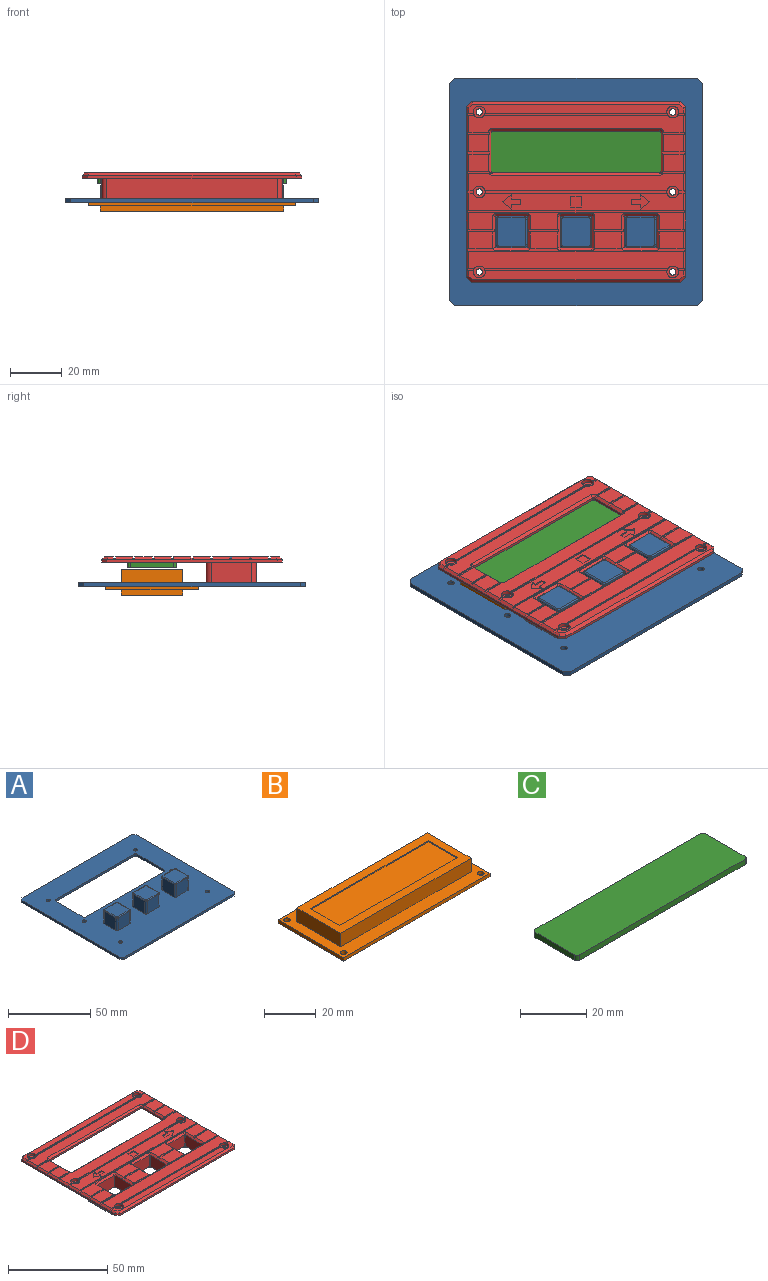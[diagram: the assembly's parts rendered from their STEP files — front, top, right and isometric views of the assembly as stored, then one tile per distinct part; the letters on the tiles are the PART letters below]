
ASSEMBLY  parts=4 mates=3
PART A: 75 faces, bbox 98x88x11.6 mm
  f0: plane 98x88mm, normal (0,0,1), area 6339.1mm2, adj f2,f3,f4,f5,f6,f7,f8,f9
  f1: plane 98x88mm, normal (0,0,-1), area 6768.5mm2, adj f2,f3,f4,f5,f6,f7,f8,f9
  f2: plane 94x1.6mm, normal (0,-1,0), area 150.4mm2, adj f0,f1,f64,f65
  f3: plane 84x1.6mm, normal (1,0,0), area 134.4mm2, adj f0,f1,f65,f66
  f4: plane 94x1.6mm, normal (0,1,0), area 150.4mm2, adj f0,f1,f63,f66
  f5: plane 84x1.6mm, normal (-1,0,0), area 134.4mm2, adj f0,f1,f63,f64
  f6: cylinder r=1.25mm len=2.5mm, axis (0,0,1), area 12.6mm2, adj f0,f1
  f7: cylinder r=1.25mm len=2.5mm, axis (0,0,1), area 12.6mm2, adj f0,f1
  f8: cylinder r=1.25mm len=2.5mm, axis (0,0,1), area 12.6mm2, adj f0,f1
  f9: cylinder r=1.25mm len=2.5mm, axis (0,0,1), area 12.6mm2, adj f0,f1
  f10: cylinder r=1.25mm len=2.5mm, axis (0,0,1), area 12.6mm2, adj f0,f1
  f11: cylinder r=1.25mm len=2.5mm, axis (0,0,1), area 12.6mm2, adj f0,f1
  f12: plane 10x9.5mm, normal (0,-1,0), area 95mm2, adj f0,f35,f38,f45
  f13: plane 10x9.5mm, normal (1,0,0), area 95mm2, adj f0,f37,f38,f41
  f14: plane 10x9.5mm, normal (0,1,0), area 95mm2, adj f0,f36,f37,f40
  f15: plane 10x9.5mm, normal (-1,0,0), area 95mm2, adj f0,f35,f36,f44
  f16: plane 11x11mm, normal (0,0,1), area 120.8mm2, adj f39,f40,f41,f42,f43,f44,f45,f46
  f17: plane 10x9.5mm, normal (-1,0,0), area 95mm2, adj f0,f31,f34,f52
  f18: plane 10x9.5mm, normal (0,-1,0), area 95mm2, adj f0,f31,f32,f53
  f19: plane 10x9.5mm, normal (1,0,0), area 95mm2, adj f0,f32,f33,f49
  f20: plane 10x9.5mm, normal (0,1,0), area 95mm2, adj f0,f33,f34,f48
  f21: plane 11x11mm, normal (0,0,1), area 120.8mm2, adj f47,f48,f49,f50,f51,f52,f53,f54
  f22: plane 10x9.5mm, normal (0,1,0), area 95mm2, adj f0,f27,f30,f61
  f23: plane 10x9.5mm, normal (-1,0,0), area 95mm2, adj f0,f29,f30,f57
  f24: plane 10x9.5mm, normal (0,-1,0), area 95mm2, adj f0,f28,f29,f56
  f25: plane 10x9.5mm, normal (1,0,0), area 95mm2, adj f0,f27,f28,f60
  f26: plane 11x11mm, normal (0,0,1), area 120.8mm2, adj f55,f56,f57,f58,f59,f60,f61,f62
  f27: cylinder r=1mm len=9.5mm, axis (0,0,-1), area 14.9mm2, adj f0,f22,f25,f62
  f28: cylinder r=1mm len=9.5mm, axis (0,0,1), area 14.9mm2, adj f0,f24,f25,f58
  f29: cylinder r=1mm len=9.5mm, axis (0,0,-1), area 14.9mm2, adj f0,f23,f24,f55
  f30: cylinder r=1mm len=9.5mm, axis (0,0,1), area 14.9mm2, adj f0,f22,f23,f59
  f31: cylinder r=1mm len=9.5mm, axis (0,0,1), area 14.9mm2, adj f0,f17,f18,f54
  f32: cylinder r=1mm len=9.5mm, axis (0,0,-1), area 14.9mm2, adj f0,f18,f19,f51
  f33: cylinder r=1mm len=9.5mm, axis (0,0,1), area 14.9mm2, adj f0,f19,f20,f47
  f34: cylinder r=1mm len=9.5mm, axis (0,0,-1), area 14.9mm2, adj f0,f17,f20,f50
  f35: cylinder r=1mm len=9.5mm, axis (0,0,-1), area 14.9mm2, adj f0,f12,f15,f46
  f36: cylinder r=1mm len=9.5mm, axis (0,0,1), area 14.9mm2, adj f0,f14,f15,f42
  f37: cylinder r=1mm len=9.5mm, axis (0,0,-1), area 14.9mm2, adj f0,f13,f14,f39
  f38: cylinder r=1mm len=9.5mm, axis (0,0,1), area 14.9mm2, adj f0,f12,f13,f43
  f39: torus R=0.5mm, axis (0,0,1), area 1mm2, adj f16,f37,f40,f41
  f40: cylinder r=0.5mm len=10mm, axis (1,0,0), area 7.9mm2, adj f14,f16,f39,f42
  f41: cylinder r=0.5mm len=10mm, axis (0,-1,0), area 7.9mm2, adj f13,f16,f39,f43
  f42: torus R=0.5mm, axis (0,0,1), area 1mm2, adj f16,f36,f40,f44
  f43: torus R=0.5mm, axis (0,0,1), area 1mm2, adj f16,f38,f41,f45
  f44: cylinder r=0.5mm len=10mm, axis (0,1,0), area 7.9mm2, adj f15,f16,f42,f46
  f45: cylinder r=0.5mm len=10mm, axis (-1,0,0), area 7.9mm2, adj f12,f16,f43,f46
  f46: torus R=0.5mm, axis (0,0,1), area 1mm2, adj f16,f35,f44,f45
  f47: torus R=0.5mm, axis (0,0,1), area 1mm2, adj f21,f33,f48,f49
  f48: cylinder r=0.5mm len=10mm, axis (1,0,0), area 7.9mm2, adj f20,f21,f47,f50
  f49: cylinder r=0.5mm len=10mm, axis (0,-1,0), area 7.9mm2, adj f19,f21,f47,f51
  f50: torus R=0.5mm, axis (0,0,1), area 1mm2, adj f21,f34,f48,f52
  f51: torus R=0.5mm, axis (0,0,1), area 1mm2, adj f21,f32,f49,f53
  f52: cylinder r=0.5mm len=10mm, axis (0,1,0), area 7.9mm2, adj f17,f21,f50,f54
  f53: cylinder r=0.5mm len=10mm, axis (-1,0,0), area 7.9mm2, adj f18,f21,f51,f54
  f54: torus R=0.5mm, axis (0,0,1), area 1mm2, adj f21,f31,f52,f53
  f55: torus R=0.5mm, axis (0,0,1), area 1mm2, adj f26,f29,f56,f57
  f56: cylinder r=0.5mm len=10mm, axis (-1,0,0), area 7.9mm2, adj f24,f26,f55,f58
  f57: cylinder r=0.5mm len=10mm, axis (0,1,0), area 7.9mm2, adj f23,f26,f55,f59
  f58: torus R=0.5mm, axis (0,0,1), area 1mm2, adj f26,f28,f56,f60
  f59: torus R=0.5mm, axis (0,0,1), area 1mm2, adj f26,f30,f57,f61
  f60: cylinder r=0.5mm len=10mm, axis (0,-1,0), area 7.9mm2, adj f25,f26,f58,f62
  f61: cylinder r=0.5mm len=10mm, axis (1,0,0), area 7.9mm2, adj f22,f26,f59,f62
  f62: torus R=0.5mm, axis (0,0,1), area 1mm2, adj f26,f27,f60,f61
  f63: plane 2x2mm, normal (-0.71,0.71,0), area 4.5mm2, adj f0,f1,f4,f5
  f64: plane 2x2mm, normal (-0.71,-0.71,0), area 4.5mm2, adj f0,f1,f2,f5
  f65: plane 2x2mm, normal (0.71,-0.71,0), area 4.5mm2, adj f0,f1,f2,f3
  f66: plane 2x2mm, normal (0.71,0.71,0), area 4.5mm2, adj f0,f1,f3,f4
  f67: plane 68x1.6mm, normal (0,1,0), area 108.8mm2, adj f0,f1,f71,f72
  f68: plane 24x1.6mm, normal (-1,0,0), area 38.4mm2, adj f0,f1,f72,f73
  f69: plane 68x1.6mm, normal (0,-1,0), area 108.8mm2, adj f0,f1,f73,f74
  f70: plane 24x1.6mm, normal (1,0,0), area 38.4mm2, adj f0,f1,f71,f74
  f71: plane 1.6x1mm, normal (0.71,0.71,0), area 2.3mm2, adj f0,f1,f67,f70
  f72: plane 1.6x1mm, normal (-0.71,0.71,0), area 2.3mm2, adj f0,f1,f67,f68
  f73: plane 1.6x1mm, normal (-0.71,-0.71,0), area 2.3mm2, adj f0,f1,f68,f69
  f74: plane 1.6x1mm, normal (0.71,-0.71,0), area 2.3mm2, adj f0,f1,f69,f70
PART B: 25 faces, bbox 80x36x10 mm
  f0: plane 71.3x24mm, normal (0,0,1), area 679.2mm2, adj f11,f12,f13,f14,f15,f16,f17,f18
  f1: plane 80x36mm, normal (0,0,1), area 1149.2mm2, adj f2,f3,f4,f5,f7,f8,f9,f10
  f2: plane 80x1.6mm, normal (0,-1,0), area 128mm2, adj f1,f3,f5,f6
  f3: plane 36x1.6mm, normal (1,0,0), area 57.6mm2, adj f1,f2,f4,f6
  f4: plane 80x1.6mm, normal (0,1,0), area 128mm2, adj f1,f3,f5,f6
  f5: plane 36x1.6mm, normal (-1,0,0), area 57.6mm2, adj f1,f2,f4,f6
  f6: plane 80x36mm, normal (0,0,-1), area 1156.4mm2, adj f2,f3,f4,f5,f7,f8,f9,f10
  f7: cylinder r=1.25mm len=2.5mm, axis (0,0,1), area 12.6mm2, adj f1,f6
  f8: cylinder r=1.25mm len=2.5mm, axis (0,0,1), area 12.6mm2, adj f1,f6
  f9: cylinder r=1.25mm len=2.5mm, axis (0,0,1), area 12.6mm2, adj f1,f6
  f10: cylinder r=1.25mm len=2.5mm, axis (0,0,1), area 12.6mm2, adj f1,f6
  f11: plane 24x6.4mm, normal (-1,0,0), area 153.6mm2, adj f0,f1,f12,f14
  f12: plane 71.3x6.4mm, normal (0,-1,0), area 456.3mm2, adj f0,f1,f11,f13
  f13: plane 24x6.4mm, normal (1,0,0), area 153.6mm2, adj f0,f1,f12,f14
  f14: plane 71.3x6.4mm, normal (0,1,0), area 456.3mm2, adj f0,f1,f11,f13
  f15: plane 16x0.5mm, normal (1,0,0), area 8mm2, adj f0,f16,f18,f19
  f16: plane 64.5x0.5mm, normal (0,1,0), area 32.3mm2, adj f0,f15,f17,f19
  f17: plane 16x0.5mm, normal (-1,0,0), area 8mm2, adj f0,f16,f18,f19
  f18: plane 64.5x0.5mm, normal (0,-1,0), area 32.3mm2, adj f0,f15,f17,f19
  f19: plane 64.5x16mm, normal (0,0,1), area 1032mm2, adj f15,f16,f17,f18
  f20: plane 24x2mm, normal (-1,0,0), area 48mm2, adj f6,f21,f23,f24
  f21: plane 71x2mm, normal (0,1,0), area 142mm2, adj f6,f20,f22,f24
  f22: plane 24x2mm, normal (1,0,0), area 48mm2, adj f6,f21,f23,f24
  f23: plane 71x2mm, normal (0,-1,0), area 142mm2, adj f6,f20,f22,f24
  f24: plane 71x24mm, normal (0,0,-1), area 1704mm2, adj f20,f21,f22,f23
PART C: 10 faces, bbox 73x19x2 mm
  f0: plane 71x2mm, normal (0,-1,0), area 142mm2, adj f4,f5,f6,f9
  f1: plane 17x2mm, normal (1,0,0), area 34mm2, adj f4,f5,f6,f7
  f2: plane 71x2mm, normal (0,1,0), area 142mm2, adj f4,f5,f7,f8
  f3: plane 17x2mm, normal (-1,0,0), area 34mm2, adj f4,f5,f8,f9
  f4: plane 73x19mm, normal (0,0,1), area 1386.1mm2, adj f0,f1,f2,f3,f6,f7,f8,f9
  f5: plane 73x19mm, normal (0,0,-1), area 1386.1mm2, adj f0,f1,f2,f3,f6,f7,f8,f9
  f6: cylinder r=1mm len=2mm, axis (0,0,1), area 3.1mm2, adj f0,f1,f4,f5
  f7: cylinder r=1mm len=2mm, axis (0,0,-1), area 3.1mm2, adj f1,f2,f4,f5
  f8: cylinder r=1mm len=2mm, axis (0,0,1), area 3.1mm2, adj f2,f3,f4,f5
  f9: cylinder r=1mm len=2mm, axis (0,0,-1), area 3.1mm2, adj f0,f3,f4,f5
PART D: 243 faces, bbox 85x70x10 mm
  f0: plane 15.5x8mm, normal (1,0,0), area 124mm2, adj f33,f111,f216,f242
  f1: plane 15.5x8mm, normal (-1,0,0), area 124mm2, adj f33,f112,f216,f241
  f2: plane 65x1mm, normal (0,1,0), area 65mm2, adj f6,f9,f33,f105
  f3: plane 15x1mm, normal (-1,0,0), area 15mm2, adj f6,f7,f33,f101
  f4: plane 65x1mm, normal (0,-1,0), area 65mm2, adj f7,f8,f33,f100
  f5: plane 15x1mm, normal (1,0,0), area 15mm2, adj f8,f9,f33,f102
  f6: cylinder r=0.5mm len=1mm, axis (0,0,1), area 0.8mm2, adj f2,f3,f33,f103
  f7: cylinder r=0.5mm len=1mm, axis (0,0,-1), area 0.8mm2, adj f3,f4,f28,f33
  f8: cylinder r=0.5mm len=1mm, axis (0,0,1), area 0.8mm2, adj f4,f5,f29,f33
  f9: cylinder r=0.5mm len=1mm, axis (0,0,-1), area 0.8mm2, adj f2,f5,f33,f104
  f10: plane 83x6.62mm, normal (0,0,1), area 544.7mm2, adj f24,f25,f30,f31,f174,f178,f199,f212
  f11: plane 9.39x6.62mm, normal (0,0,1), area 61.3mm2, adj f30,f79,f81,f161,f196
  f12: plane 10.78x6.62mm, normal (0,0,1), area 69.6mm2, adj f80,f82,f87,f89,f165,f203
  f13: plane 10.78x6.62mm, normal (0,0,1), area 69.6mm2, adj f88,f90,f96,f98,f169,f202
  f14: plane 9.39x6.62mm, normal (0,0,1), area 61.3mm2, adj f31,f95,f97,f160,f173
  f15: plane 83x6.62mm, normal (0,0,1), area 275.5mm2, adj f30,f31,f76,f77,f78,f79,f80,f84
  f16: plane 83x6.62mm, normal (0,0,1), area 487.1mm2, adj f26,f27,f30,f31,f119,f120,f121,f122
  f17: plane 83x6.62mm, normal (0,0,1), area 499mm2, adj f26,f27,f30,f31,f103,f104,f105,f151
  f18: plane 7.5x6.62mm, normal (0,0,1), area 49.7mm2, adj f31,f102,f104,f148,f150
  f19: plane 7.5x6.62mm, normal (0,0,1), area 49.7mm2, adj f30,f101,f103,f185,f189
  f20: plane 7.5x6.62mm, normal (0,0,1), area 49.7mm2, adj f31,f102,f144,f147
  f21: plane 7.5x6.62mm, normal (0,0,1), area 49.6mm2, adj f30,f101,f183,f186
  f22: plane 83x6.62mm, normal (0,0,1), area 444.3mm2, adj f28,f29,f30,f31,f40,f51,f100,f142
  f23: plane 83x3.47mm, normal (0,0,1), area 265.1mm2, adj f30,f31,f40,f51,f115,f117,f118,f141
  f24: cylinder r=2.3mm len=4.6mm, axis (0,0,1), area 20.7mm2, adj f10,f32,f42,f197,f198,f199,f212,f213
  f25: cylinder r=2.3mm len=4.6mm, axis (0,0,1), area 20.7mm2, adj f10,f32,f44,f176,f177,f178,f212,f213
  f26: cylinder r=2.3mm len=4.6mm, axis (0,0,1), area 20.8mm2, adj f16,f17,f46,f152,f153,f154,f209,f210
  f27: cylinder r=2.3mm len=4.6mm, axis (0,0,1), area 20.8mm2, adj f16,f17,f48,f191,f192,f193,f209,f210
  f28: cone r=1.5mm half-angle=45deg, axis (0,0,1), area 2.2mm2, adj f7,f22,f100,f101,f182,f184
  f29: cone r=1.5mm half-angle=45deg, axis (0,0,1), area 2.2mm2, adj f8,f22,f100,f102,f143,f145
  f30: plane 66x1mm, normal (0.71,0,0.71), area 87mm2, adj f10,f11,f15,f16,f17,f19,f21,f22
  f31: plane 66x1mm, normal (-0.71,0,0.71), area 87mm2, adj f10,f14,f15,f16,f17,f18,f20,f22
  f32: plane 83x3.47mm, normal (0,0,1), area 265.1mm2, adj f24,f25,f30,f31,f113,f114,f116,f177
  f33: plane 85x70mm, normal (0,0,-1), area 3495.2mm2, adj f0,f1,f2,f3,f4,f5,f6,f7
  f34: plane 81x1mm, normal (0,-1,0), area 81mm2, adj f33,f108,f109,f114
  f35: plane 66x1mm, normal (1,0,0), area 66mm2, adj f30,f33,f106,f109
  f36: plane 81x1mm, normal (0,1,0), area 81mm2, adj f33,f106,f107,f117
  f37: plane 66x1mm, normal (-1,0,0), area 66mm2, adj f31,f33,f107,f108
  f38: cylinder r=1.25mm len=2.5mm, axis (0,0,1), area 3.9mm2, adj f33,f39
  f39: plane 4.6x4.6mm, normal (0,0,1), area 11.7mm2, adj f38,f40
  f40: cylinder r=2.3mm len=4.6mm, axis (0,0,1), area 20.7mm2, adj f22,f23,f39,f140,f141,f142,f206,f207
  f41: cylinder r=1.25mm len=2.5mm, axis (0,0,1), area 3.9mm2, adj f33,f42
  f42: plane 4.6x4.6mm, normal (0,0,1), area 11.7mm2, adj f24,f41
  f43: cylinder r=1.25mm len=2.5mm, axis (0,0,1), area 3.9mm2, adj f33,f44
  f44: plane 4.6x4.6mm, normal (0,0,1), area 11.7mm2, adj f25,f43
  f45: cylinder r=1.25mm len=2.5mm, axis (0,0,1), area 3.9mm2, adj f33,f46
  f46: plane 4.6x4.6mm, normal (0,0,1), area 11.7mm2, adj f26,f45
  f47: cylinder r=1.25mm len=2.5mm, axis (0,0,1), area 3.9mm2, adj f33,f48
  f48: plane 4.6x4.6mm, normal (0,0,1), area 11.7mm2, adj f27,f47
  f49: cylinder r=1.25mm len=2.5mm, axis (0,0,1), area 3.9mm2, adj f33,f50
  f50: plane 4.6x4.6mm, normal (0,0,1), area 11.7mm2, adj f49,f51
  f51: cylinder r=2.3mm len=4.6mm, axis (0,0,1), area 20.7mm2, adj f22,f23,f50,f179,f180,f181,f206,f207
  f52: plane 12.1x7mm, normal (0,1,0), area 84.7mm2, adj f64,f67,f83,f236
  f53: plane 12.1x7mm, normal (-1,0,0), area 84.7mm2, adj f66,f67,f79,f233
  f54: plane 12.1x7mm, normal (0,-1,0), area 84.7mm2, adj f65,f66,f76,f237
  f55: plane 12.1x7mm, normal (1,0,0), area 84.7mm2, adj f64,f65,f80,f240
  f56: plane 12.1x7mm, normal (0,1,0), area 84.7mm2, adj f68,f71,f91,f228
  f57: plane 12.1x7mm, normal (-1,0,0), area 84.7mm2, adj f68,f69,f87,f225
  f58: plane 12.1x7mm, normal (0,-1,0), area 84.7mm2, adj f69,f70,f84,f229
  f59: plane 12.1x7mm, normal (1,0,0), area 84.7mm2, adj f70,f71,f88,f232
  f60: plane 12.1x7mm, normal (-1,0,0), area 84.7mm2, adj f72,f75,f96,f217
  f61: plane 12.1x7mm, normal (0,-1,0), area 84.7mm2, adj f74,f75,f92,f221
  f62: plane 12.1x7mm, normal (1,0,0), area 84.7mm2, adj f73,f74,f95,f224
  f63: plane 12.1x7mm, normal (0,1,0), area 84.7mm2, adj f72,f73,f99,f220
  f64: cylinder r=0.2mm len=7mm, axis (0,0,-1), area 2.2mm2, adj f52,f55,f82,f238
  f65: cylinder r=0.2mm len=7mm, axis (0,0,1), area 2.2mm2, adj f54,f55,f78,f239
  f66: cylinder r=0.2mm len=7mm, axis (0,0,-1), area 2.2mm2, adj f53,f54,f77,f235
  f67: cylinder r=0.2mm len=7mm, axis (0,0,1), area 2.2mm2, adj f52,f53,f81,f234
  f68: cylinder r=0.2mm len=7mm, axis (0,0,1), area 2.2mm2, adj f56,f57,f89,f226
  f69: cylinder r=0.2mm len=7mm, axis (0,0,-1), area 2.2mm2, adj f57,f58,f85,f227
  f70: cylinder r=0.2mm len=7mm, axis (0,0,1), area 2.2mm2, adj f58,f59,f86,f231
  f71: cylinder r=0.2mm len=7mm, axis (0,0,-1), area 2.2mm2, adj f56,f59,f90,f230
  f72: cylinder r=0.2mm len=7mm, axis (0,0,-1), area 2.2mm2, adj f60,f63,f98,f218
  f73: cylinder r=0.2mm len=7mm, axis (0,0,1), area 2.2mm2, adj f62,f63,f97,f222
  f74: cylinder r=0.2mm len=7mm, axis (0,0,1), area 2.2mm2, adj f61,f62,f93,f223
  f75: cylinder r=0.2mm len=7mm, axis (0,0,-1), area 2.2mm2, adj f60,f61,f94,f219
  f76: plane 12.1x1mm, normal (0,-0.71,0.71), area 17.1mm2, adj f15,f54,f77,f78
  f77: cone r=1.2mm half-angle=45deg, axis (0,0,1), area 1.6mm2, adj f15,f66,f76,f79
  f78: cone r=1.2mm half-angle=45deg, axis (0,0,1), area 1.6mm2, adj f15,f65,f76,f80
  f79: plane 12.1x1mm, normal (-0.71,0,0.71), area 16.5mm2, adj f11,f15,f53,f77,f81,f194,f195,f196
  f80: plane 12.1x1mm, normal (0.71,0,0.71), area 16.5mm2, adj f12,f15,f55,f78,f82,f203,f204,f205
  f81: cone r=1.2mm half-angle=45deg, axis (0,0,1), area 1.6mm2, adj f11,f67,f79,f83,f162
  f82: cone r=1.2mm half-angle=45deg, axis (0,0,1), area 1.6mm2, adj f12,f64,f80,f83,f164
  f83: plane 12.1x1mm, normal (0,0.71,0.71), area 17.1mm2, adj f52,f81,f82,f163
  f84: plane 12.1x1mm, normal (0,-0.71,0.71), area 17.1mm2, adj f15,f58,f85,f86
  f85: cone r=1.2mm half-angle=45deg, axis (0,0,1), area 1.6mm2, adj f15,f69,f84,f87
  f86: cone r=1.2mm half-angle=45deg, axis (0,0,1), area 1.6mm2, adj f15,f70,f84,f88
  f87: plane 12.1x1mm, normal (-0.71,0,0.71), area 16.5mm2, adj f12,f15,f57,f85,f89,f203,f204,f205
  f88: plane 12.1x1mm, normal (0.71,0,0.71), area 16.5mm2, adj f13,f15,f59,f86,f90,f200,f201,f202
  f89: cone r=1.2mm half-angle=45deg, axis (0,0,1), area 1.6mm2, adj f12,f68,f87,f91,f166
  f90: cone r=1.2mm half-angle=45deg, axis (0,0,1), area 1.6mm2, adj f13,f71,f88,f91,f168
  f91: plane 12.1x1mm, normal (0,0.71,0.71), area 17.1mm2, adj f56,f89,f90,f167
  f92: plane 12.1x1mm, normal (0,-0.71,0.71), area 17.1mm2, adj f15,f61,f93,f94
  f93: cone r=1.2mm half-angle=45deg, axis (0,0,1), area 1.6mm2, adj f15,f74,f92,f95
  f94: cone r=1.2mm half-angle=45deg, axis (0,0,1), area 1.6mm2, adj f15,f75,f92,f96
  f95: plane 12.1x1mm, normal (0.71,0,0.71), area 16.5mm2, adj f14,f15,f62,f93,f97,f158,f159,f160
  f96: plane 12.1x1mm, normal (-0.71,0,0.71), area 16.5mm2, adj f13,f15,f60,f94,f98,f200,f201,f202
  f97: cone r=1.2mm half-angle=45deg, axis (0,0,1), area 1.6mm2, adj f14,f73,f95,f99,f172
  f98: cone r=1.2mm half-angle=45deg, axis (0,0,1), area 1.6mm2, adj f13,f72,f96,f99,f170
  f99: plane 12.1x1mm, normal (0,0.71,0.71), area 17.1mm2, adj f63,f97,f98,f171
  f100: plane 65x1mm, normal (0,-0.71,0.71), area 91.9mm2, adj f4,f22,f28,f29
  f101: plane 15x1mm, normal (-0.71,0,0.71), area 19.9mm2, adj f3,f19,f21,f28,f103,f183,f184,f185
  f102: plane 15x1mm, normal (0.71,0,0.71), area 19.9mm2, adj f5,f18,f20,f29,f104,f143,f144,f146
  f103: cone r=1.5mm half-angle=45deg, axis (0,0,1), area 1.5mm2, adj f6,f17,f19,f101,f105,f188,f189,f190
  f104: cone r=1.5mm half-angle=45deg, axis (0,0,1), area 1.5mm2, adj f9,f17,f18,f102,f105,f149,f150,f151
  f105: plane 65x1mm, normal (0,0.71,0.71), area 91.9mm2, adj f2,f17,f103,f104
  f106: plane 2x2mm, normal (0.71,0.71,0), area 2.8mm2, adj f33,f35,f36,f115
  f107: plane 2x2mm, normal (-0.71,0.71,0), area 2.8mm2, adj f33,f36,f37,f118
  f108: plane 2x2mm, normal (-0.71,-0.71,0), area 2.8mm2, adj f33,f34,f37,f116
  f109: plane 2x2mm, normal (0.71,-0.71,0), area 2.8mm2, adj f33,f34,f35,f113
  f110: plane 66x8mm, normal (0,-1,0), area 528mm2, adj f33,f111,f112,f216
  f111: cylinder r=2mm len=8mm, axis (0,0,1), area 25.1mm2, adj f0,f33,f110,f216
  f112: cylinder r=2mm len=8mm, axis (0,0,-1), area 25.1mm2, adj f1,f33,f110,f216
  f113: plane 2.41x2.41mm, normal (0.5,-0.5,0.71), area 3.4mm2, adj f30,f32,f109,f114
  f114: plane 81x1mm, normal (0,-0.71,0.71), area 114mm2, adj f32,f34,f113,f116
  f115: plane 2.41x2.41mm, normal (0.5,0.5,0.71), area 3.4mm2, adj f23,f30,f106,f117
  f116: plane 2.41x2.41mm, normal (-0.5,-0.5,0.71), area 3.4mm2, adj f31,f32,f108,f114
  f117: plane 81x1mm, normal (0,0.71,0.71), area 114mm2, adj f23,f36,f115,f118
  f118: plane 2.41x2.41mm, normal (-0.5,0.5,0.71), area 3.4mm2, adj f23,f31,f107,f117
  f119: plane 3.5x2.83mm, normal (-0.63,-0.78,0), area 2.3mm2, adj f16,f120,f125,f126
  f120: plane 1.83x0.5mm, normal (1,0,0), area 0.9mm2, adj f16,f119,f121,f126
  f121: plane 3.5x0.5mm, normal (0,-1,0), area 1.8mm2, adj f16,f120,f122,f126
  f122: plane 2x0.5mm, normal (1,0,0), area 1mm2, adj f16,f121,f123,f126
  f123: plane 3.5x0.5mm, normal (0,1,0), area 1.8mm2, adj f16,f122,f124,f126
  f124: plane 1.83x0.5mm, normal (1,0,0), area 0.9mm2, adj f16,f123,f125,f126
  f125: plane 3.5x2.83mm, normal (-0.63,0.78,0), area 2.3mm2, adj f16,f119,f124,f126
  f126: plane 7x5.66mm, normal (0,0,1), area 16.9mm2, adj f119,f120,f121,f122,f123,f124,f125
  f127: plane 4x0.5mm, normal (0,1,0), area 2mm2, adj f16,f128,f130,f131
  f128: plane 4x0.5mm, normal (-1,0,0), area 2mm2, adj f16,f127,f129,f131
  f129: plane 4x0.5mm, normal (0,-1,0), area 2mm2, adj f16,f128,f130,f131
  f130: plane 4x0.5mm, normal (1,0,0), area 2mm2, adj f16,f127,f129,f131
  f131: plane 4x4mm, normal (0,0,1), area 16mm2, adj f127,f128,f129,f130
  f132: plane 3.5x0.5mm, normal (0,-1,0), area 1.8mm2, adj f16,f133,f138,f139
  f133: plane 1.83x0.5mm, normal (-1,0,0), area 0.9mm2, adj f16,f132,f134,f139
  f134: plane 3.5x2.83mm, normal (0.63,-0.78,0), area 2.3mm2, adj f16,f133,f135,f139
  f135: plane 3.5x2.83mm, normal (0.63,0.78,0), area 2.3mm2, adj f16,f134,f136,f139
  f136: plane 1.83x0.5mm, normal (-1,0,0), area 0.9mm2, adj f16,f135,f137,f139
  f137: plane 3.5x0.5mm, normal (0,1,0), area 1.8mm2, adj f16,f136,f138,f139
  f138: plane 2x0.5mm, normal (-1,0,0), area 1mm2, adj f16,f132,f137,f139
  f139: plane 7x5.66mm, normal (0,0,1), area 16.9mm2, adj f132,f133,f134,f135,f136,f137,f138
  f140: plane 2.65x0.9mm, normal (0,0,1), area 2.2mm2, adj f31,f40,f141,f142
  f141: plane 2.25x0.5mm, normal (0,-1,0), area 1mm2, adj f23,f31,f40,f140
  f142: plane 2.65x0.5mm, normal (0,1,0), area 1.2mm2, adj f22,f31,f40,f140
  f143: plane 8.5x0.9mm, normal (0,0,1), area 7.7mm2, adj f29,f31,f102,f144,f145
  f144: plane 8.5x0.5mm, normal (0,1,0), area 4mm2, adj f20,f31,f102,f143
  f145: plane 8.5x0.5mm, normal (0,-1,0), area 4mm2, adj f22,f29,f31,f143
  f146: plane 8.5x0.9mm, normal (0,0,1), area 7.6mm2, adj f31,f102,f147,f148
  f147: plane 8.5x0.5mm, normal (0,-1,0), area 4mm2, adj f20,f31,f102,f146
  f148: plane 8.5x0.5mm, normal (0,1,0), area 4mm2, adj f18,f31,f102,f146
  f149: plane 9.13x0.9mm, normal (0,0,1), area 7.8mm2, adj f31,f104,f150,f151
  f150: plane 8.5x0.5mm, normal (0,-1,0), area 4mm2, adj f18,f31,f104,f149
  f151: plane 9.13x0.5mm, normal (0,1,0), area 4.2mm2, adj f17,f31,f104,f149
  f152: plane 2.24x0.9mm, normal (0,0,1), area 2mm2, adj f26,f31,f153,f154
  f153: plane 2.24x0.5mm, normal (0,1,0), area 1mm2, adj f16,f26,f31,f152
  f154: plane 2.24x0.5mm, normal (0,-1,0), area 1mm2, adj f17,f26,f31,f152
  f155: plane 84x0.5mm, normal (0,1,0), area 41.7mm2, adj f15,f30,f31,f157
  f156: plane 84x0.5mm, normal (0,-1,0), area 41.7mm2, adj f16,f30,f31,f157
  f157: plane 84x0.9mm, normal (0,0,1), area 75.6mm2, adj f30,f31,f155,f156
  f158: plane 10.25x0.9mm, normal (0,0,1), area 9.2mm2, adj f31,f95,f159,f160
  f159: plane 10.25x0.5mm, normal (0,-1,0), area 4.9mm2, adj f15,f31,f95,f158
  f160: plane 10.25x0.5mm, normal (0,1,0), area 4.9mm2, adj f14,f31,f95,f158
  f161: plane 9.89x0.5mm, normal (0,-1,0), area 4.8mm2, adj f11,f30,f162,f175
  f162: cylinder r=1.2mm len=1.06mm, axis (0,0,1), area 0.7mm2, adj f81,f161,f163,f175
  f163: plane 12.1x0.5mm, normal (0,-1,0), area 6mm2, adj f83,f162,f164,f175
  f164: cylinder r=1.2mm len=1.06mm, axis (0,0,1), area 0.7mm2, adj f82,f163,f165,f175
  f165: plane 10.78x0.5mm, normal (0,-1,0), area 5.4mm2, adj f12,f164,f166,f175
  f166: cylinder r=1.2mm len=1.06mm, axis (0,0,1), area 0.7mm2, adj f89,f165,f167,f175
  f167: plane 12.1x0.5mm, normal (0,-1,0), area 6mm2, adj f91,f166,f168,f175
  f168: cylinder r=1.2mm len=1.06mm, axis (0,0,1), area 0.7mm2, adj f90,f167,f169,f175
  f169: plane 10.78x0.5mm, normal (0,-1,0), area 5.4mm2, adj f13,f168,f170,f175
  f170: cylinder r=1.2mm len=1.06mm, axis (0,0,1), area 0.7mm2, adj f98,f169,f171,f175
  f171: plane 12.1x0.5mm, normal (0,-1,0), area 6mm2, adj f99,f170,f172,f175
  f172: cylinder r=1.2mm len=1.06mm, axis (0,0,1), area 0.7mm2, adj f97,f171,f173,f175
  f173: plane 9.89x0.5mm, normal (0,-1,0), area 4.8mm2, adj f14,f31,f172,f175
  f174: plane 84x0.5mm, normal (0,1,0), area 41.7mm2, adj f10,f30,f31,f175
  f175: plane 84x0.9mm, normal (0,0,1), area 49.5mm2, adj f30,f31,f161,f162,f163,f164,f165,f166
  f176: plane 2.65x0.9mm, normal (0,0,1), area 2.2mm2, adj f25,f31,f177,f178
  f177: plane 2.25x0.5mm, normal (0,1,0), area 1mm2, adj f25,f31,f32,f176
  f178: plane 2.65x0.5mm, normal (0,-1,0), area 1.2mm2, adj f10,f25,f31,f176
  f179: plane 2.65x0.9mm, normal (0,0,1), area 2.2mm2, adj f30,f51,f180,f181
  f180: plane 2.25x0.5mm, normal (0,-1,0), area 1mm2, adj f23,f30,f51,f179
  f181: plane 2.65x0.5mm, normal (0,1,0), area 1.2mm2, adj f22,f30,f51,f179
  f182: plane 8.5x0.5mm, normal (0,-1,0), area 4mm2, adj f22,f28,f30,f184
  f183: plane 8.5x0.5mm, normal (0,1,0), area 4mm2, adj f21,f30,f101,f184
  f184: plane 8.5x0.9mm, normal (0,0,1), area 7.7mm2, adj f28,f30,f101,f182,f183
  f185: plane 8.5x0.5mm, normal (0,1,0), area 4mm2, adj f19,f30,f101,f187
  f186: plane 8.5x0.5mm, normal (0,-1,0), area 4mm2, adj f21,f30,f101,f187
  f187: plane 8.5x0.9mm, normal (0,0,1), area 7.6mm2, adj f30,f101,f185,f186
  f188: plane 9.13x0.5mm, normal (0,1,0), area 4.2mm2, adj f17,f30,f103,f190
  f189: plane 8.5x0.5mm, normal (0,-1,0), area 4mm2, adj f19,f30,f103,f190
  f190: plane 9.13x0.9mm, normal (0,0,1), area 7.8mm2, adj f30,f103,f188,f189
  f191: plane 2.24x0.9mm, normal (0,0,1), area 2mm2, adj f27,f30,f192,f193
  f192: plane 2.24x0.5mm, normal (0,1,0), area 1mm2, adj f16,f27,f30,f191
  f193: plane 2.24x0.5mm, normal (0,-1,0), area 1mm2, adj f17,f27,f30,f191
  f194: plane 10.25x0.9mm, normal (0,0,1), area 9.2mm2, adj f30,f79,f195,f196
  f195: plane 10.25x0.5mm, normal (0,-1,0), area 4.9mm2, adj f15,f30,f79,f194
  f196: plane 10.25x0.5mm, normal (0,1,0), area 4.9mm2, adj f11,f30,f79,f194
  f197: plane 2.65x0.9mm, normal (0,0,1), area 2.2mm2, adj f24,f30,f198,f199
  f198: plane 2.25x0.5mm, normal (0,1,0), area 1mm2, adj f24,f30,f32,f197
  f199: plane 2.65x0.5mm, normal (0,-1,0), area 1.2mm2, adj f10,f24,f30,f197
  f200: plane 11.5x0.9mm, normal (0,0,1), area 10.3mm2, adj f88,f96,f201,f202
  f201: plane 11.5x0.5mm, normal (0,-1,0), area 5.5mm2, adj f15,f88,f96,f200
  f202: plane 11.5x0.5mm, normal (0,1,0), area 5.5mm2, adj f13,f88,f96,f200
  f203: plane 11.5x0.5mm, normal (0,1,0), area 5.5mm2, adj f12,f80,f87,f205
  f204: plane 11.5x0.5mm, normal (0,-1,0), area 5.5mm2, adj f15,f80,f87,f205
  f205: plane 11.5x0.9mm, normal (0,0,1), area 10.3mm2, adj f80,f87,f203,f204
  f206: plane 71.31x0.5mm, normal (0,1,0), area 35.7mm2, adj f22,f40,f51,f208
  f207: plane 70.5x0.5mm, normal (0,-1,0), area 35.2mm2, adj f23,f40,f51,f208
  f208: plane 71.31x0.9mm, normal (0,0,1), area 63.7mm2, adj f40,f51,f206,f207
  f209: plane 70.49x0.5mm, normal (0,-1,0), area 35.2mm2, adj f17,f26,f27,f211
  f210: plane 70.49x0.5mm, normal (0,1,0), area 35.2mm2, adj f16,f26,f27,f211
  f211: plane 70.49x0.9mm, normal (0,0,1), area 63.4mm2, adj f26,f27,f209,f210
  f212: plane 71.31x0.5mm, normal (0,-1,0), area 35.7mm2, adj f10,f24,f25,f214
  f213: plane 70.5x0.5mm, normal (0,1,0), area 35.2mm2, adj f24,f25,f32,f214
  f214: plane 71.31x0.9mm, normal (0,0,1), area 63.7mm2, adj f24,f25,f212,f213
  f215: plane 66x8mm, normal (0,1,0), area 528mm2, adj f33,f216,f241,f242
  f216: plane 70x19.5mm, normal (0,0,-1), area 557.3mm2, adj f0,f1,f110,f111,f112,f215,f217,f218
  f217: plane 12.1x2mm, normal (-0.71,0,-0.71), area 34.2mm2, adj f60,f216,f218,f219
  f218: cone r=2.2mm half-angle=45deg, axis (0,0,-1), area 5.3mm2, adj f72,f216,f217,f220
  f219: cone r=2.2mm half-angle=45deg, axis (0,0,-1), area 5.3mm2, adj f75,f216,f217,f221
  f220: plane 12.1x2mm, normal (0,0.71,-0.71), area 34.2mm2, adj f63,f216,f218,f222
  f221: plane 12.1x2mm, normal (0,-0.71,-0.71), area 34.2mm2, adj f61,f216,f219,f223
  f222: cone r=2.2mm half-angle=45deg, axis (0,0,-1), area 5.3mm2, adj f73,f216,f220,f224
  f223: cone r=2.2mm half-angle=45deg, axis (0,0,-1), area 5.3mm2, adj f74,f216,f221,f224
  f224: plane 12.1x2mm, normal (0.71,0,-0.71), area 34.2mm2, adj f62,f216,f222,f223
  f225: plane 12.1x2mm, normal (-0.71,0,-0.71), area 34.2mm2, adj f57,f216,f226,f227
  f226: cone r=2.2mm half-angle=45deg, axis (0,0,-1), area 5.3mm2, adj f68,f216,f225,f228
  f227: cone r=2.2mm half-angle=45deg, axis (0,0,-1), area 5.3mm2, adj f69,f216,f225,f229
  f228: plane 12.1x2mm, normal (0,0.71,-0.71), area 34.2mm2, adj f56,f216,f226,f230
  f229: plane 12.1x2mm, normal (0,-0.71,-0.71), area 34.2mm2, adj f58,f216,f227,f231
  f230: cone r=2.2mm half-angle=45deg, axis (0,0,-1), area 5.3mm2, adj f71,f216,f228,f232
  f231: cone r=2.2mm half-angle=45deg, axis (0,0,-1), area 5.3mm2, adj f70,f216,f229,f232
  f232: plane 12.1x2mm, normal (0.71,0,-0.71), area 34.2mm2, adj f59,f216,f230,f231
  f233: plane 12.1x2mm, normal (-0.71,0,-0.71), area 34.2mm2, adj f53,f216,f234,f235
  f234: cone r=2.2mm half-angle=45deg, axis (0,0,-1), area 5.3mm2, adj f67,f216,f233,f236
  f235: cone r=2.2mm half-angle=45deg, axis (0,0,-1), area 5.3mm2, adj f66,f216,f233,f237
  f236: plane 12.1x2mm, normal (0,0.71,-0.71), area 34.2mm2, adj f52,f216,f234,f238
  f237: plane 12.1x2mm, normal (0,-0.71,-0.71), area 34.2mm2, adj f54,f216,f235,f239
  f238: cone r=2.2mm half-angle=45deg, axis (0,0,-1), area 5.3mm2, adj f64,f216,f236,f240
  f239: cone r=2.2mm half-angle=45deg, axis (0,0,-1), area 5.3mm2, adj f65,f216,f237,f240
  f240: plane 12.1x2mm, normal (0.71,0,-0.71), area 34.2mm2, adj f55,f216,f238,f239
  f241: cylinder r=2mm len=8mm, axis (0,0,-1), area 25.1mm2, adj f1,f33,f215,f216
  f242: cylinder r=2mm len=8mm, axis (0,0,1), area 25.1mm2, adj f0,f33,f215,f216
PLACE A t=(79.16,-56.6,4.26)mm
PLACE B t=(79.16,-41.1,3.06)mm
PLACE C t=(79.16,-41.1,11.86)mm
PLACE D t=(79.16,-56.6,13.86)mm
MATE fastened D.f49 <-> B.f8  axis (0,0,-1) through (116.66,-25.6,13.86)mm
MATE fastened D.f24 <-> A.f10  axis (0,0,-1) through (116.66,-87.6,13.86)mm
MATE fastened D.f33 <-> C.f4  axis (0,0,-1) through (79.16,-41.1,13.86)mm
